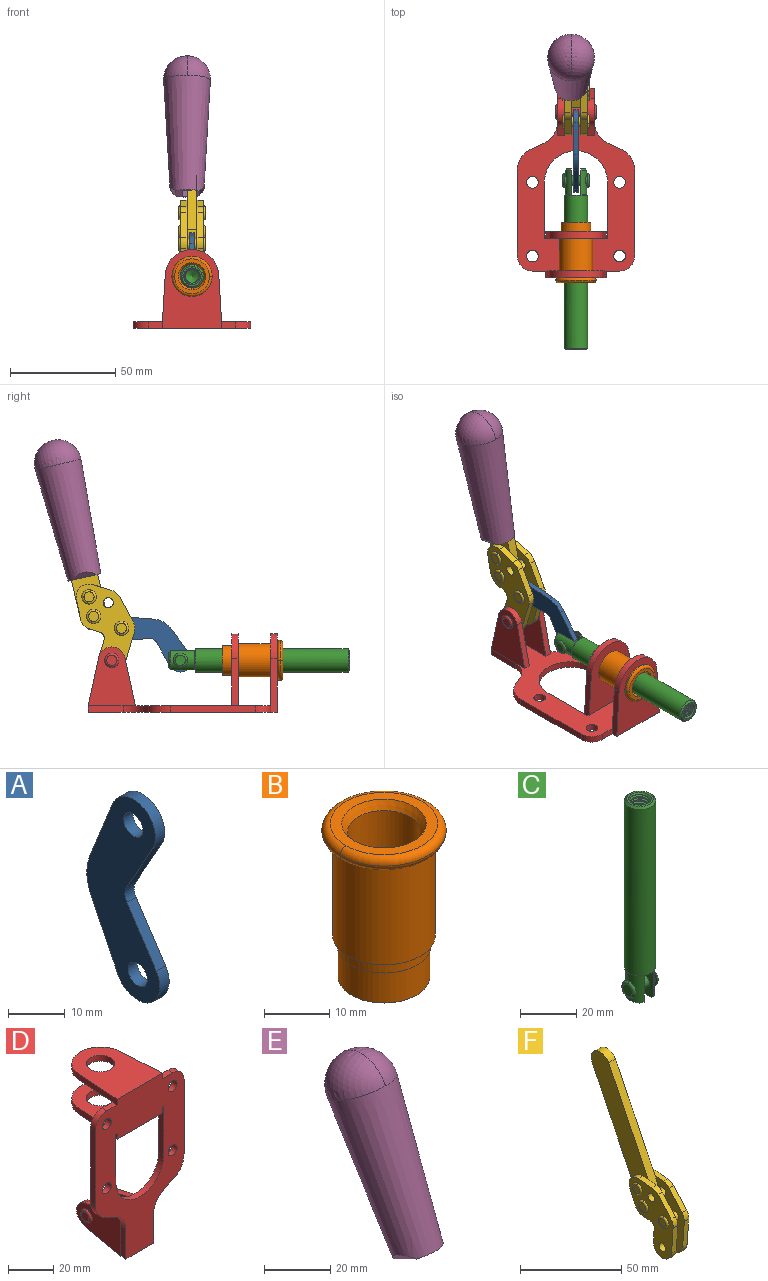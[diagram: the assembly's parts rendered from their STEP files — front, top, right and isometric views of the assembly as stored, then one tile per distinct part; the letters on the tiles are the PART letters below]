
ASSEMBLY  parts=6 mates=6
PART A: 12 faces, bbox 2.3x18.2x42.8 mm
  f0: cylinder r=2.4mm len=4.8mm, axis (1,0,0), area 34.9mm2, adj f4,f11
  f1: cylinder r=10.41mm len=8.47mm, axis (1,0,0), area 20.2mm2, adj f4,f9,f10,f11
  f2: cylinder r=3.05mm len=3.16mm, axis (1,0,0), area 7.7mm2, adj f4,f6,f7,f11
  f3: cylinder r=2.4mm len=4.8mm, axis (1,0,0), area 34.9mm2, adj f4,f11
  f4: plane 42.81x18.23mm, normal (-1,0,0), area 414.1mm2, adj f0,f1,f2,f3,f5,f6,f7,f8
  f5: cylinder r=5.54mm len=10.67mm, axis (1,0,0), area 41.8mm2, adj f4,f6,f10,f11
  f6: plane 11.66x6.53mm, normal (0,-0.87,-0.49), area 30.9mm2, adj f2,f4,f5,f11
  f7: plane 11.17x7.33mm, normal (0,-0.84,0.55), area 30.9mm2, adj f2,f4,f8,f11
  f8: cylinder r=5.54mm len=10.51mm, axis (1,0,0), area 41.8mm2, adj f4,f7,f9,f11
  f9: plane 13.67x6.67mm, normal (0,0.9,-0.44), area 35.1mm2, adj f1,f4,f8,f11
  f10: plane 14.1x5.7mm, normal (0,0.93,0.37), area 35.1mm2, adj f1,f4,f5,f11
  f11: plane 42.81x18.23mm, normal (1,0,0), area 414.1mm2, adj f0,f1,f2,f3,f5,f6,f7,f8
PART B: 15 faces, bbox 20.6x20.6x28.7 mm
  f0: torus R=8.26mm, axis (0,0,1), area 56.8mm2, adj f1,f10,f12
  f1: torus R=8.26mm, axis (0,0,1), area 56.8mm2, adj f0,f6,f13
  f2: cylinder r=5.59mm len=25.91mm, axis (0,0,1), area 909.6mm2, adj f3,f4
  f3: cone r=6.86mm half-angle=45deg, axis (0,0,-1), area 70.2mm2, adj f2,f14
  f4: cone r=6.47mm half-angle=30deg, axis (0,0,1), area 66.7mm2, adj f2,f13
  f5: cylinder r=7.04mm len=14.07mm, axis (0,0,1), area 252.6mm2, adj f11,f14
  f6: torus R=8.26mm, axis (0,0,1), area 56.8mm2, adj f1,f12,f13
  f7: cylinder r=7.16mm len=14.33mm, axis (0,0,1), area 91.5mm2, adj f9,f11
  f8: cylinder r=7.86mm len=18.42mm, axis (0,0,1), area 909.6mm2, adj f9,f10
  f9: plane 15.72x15.72mm, normal (0,0,-1), area 33mm2, adj f7,f8
  f10: plane 16.51x16.51mm, normal (0,0,-1), area 19.9mm2, adj f0,f8,f12
  f11: plane 14.33x14.33mm, normal (0,0,-1), area 5.7mm2, adj f5,f7
  f12: torus R=8.26mm, axis (0,0,1), area 56.8mm2, adj f0,f6,f10
  f13: plane 16.51x16.51mm, normal (0,0,1), area 82.7mm2, adj f1,f4,f6
  f14: plane 14.07x14.07mm, normal (0,0,-1), area 7.8mm2, adj f3,f5
PART C: 48 faces, bbox 12.6x11.1x86.1 mm
  f0: torus R=2.41mm, axis (-1,0,0), area 15mm2, adj f30,f32,f34
  f1: torus R=2.41mm, axis (-1,0,0), area 15mm2, adj f29,f31,f33
  f2: cylinder r=5.54mm len=72.39mm, axis (0,0,1), area 2518.5mm2, adj f3,f4,f42,f43
  f3: cone r=5.54mm half-angle=45deg, axis (0,0,1), area 7.6mm2, adj f2,f5,f41
  f4: cone r=5.54mm half-angle=45deg, axis (0,0,-1), area 34.9mm2, adj f2,f39
  f5: cylinder r=5.08mm len=11.48mm, axis (0,0,1), area 108.3mm2, adj f3,f7,f8,f41
  f6: cylinder r=2.41mm len=4.83mm, axis (-1,0,0), area 71.2mm2, adj f40,f41
  f7: cylinder r=2.41mm len=4.83mm, axis (-1,0,0), area 7.6mm2, adj f5,f34
  f8: cone r=5.08mm half-angle=45deg, axis (0,0,1), area 10.6mm2, adj f5,f37,f41
  f9: cone r=3.98mm half-angle=45deg, axis (0,0,1), area 17.6mm2, adj f27,f39,f45,f46,f47
  f10: cylinder r=2.41mm len=4.83mm, axis (-1,0,0), area 7.6mm2, adj f33,f38
  f11: cylinder r=3.2mm len=6.4mm, axis (0,0,1), area 78.4mm2, adj f12,f28,f44,f45,f47
  f12: cylinder r=3.2mm len=6.4mm, axis (0,0,1), area 10.5mm2, adj f11,f13,f45,f47
  f13: cylinder r=3.2mm len=6.4mm, axis (0,0,1), area 10.5mm2, adj f12,f14,f45,f47
  f14: cylinder r=3.2mm len=6.4mm, axis (0,0,1), area 10.5mm2, adj f13,f15,f45,f47
  f15: cylinder r=3.2mm len=6.4mm, axis (0,0,1), area 10.5mm2, adj f14,f16,f45,f47
  f16: cylinder r=3.2mm len=6.4mm, axis (0,0,1), area 10.5mm2, adj f15,f17,f45,f47
  f17: cylinder r=3.2mm len=6.4mm, axis (0,0,1), area 10.5mm2, adj f16,f18,f45,f47
  f18: cylinder r=3.2mm len=6.4mm, axis (0,0,1), area 10.5mm2, adj f17,f19,f45,f47
  f19: cylinder r=3.2mm len=6.4mm, axis (0,0,1), area 10.5mm2, adj f18,f20,f45,f47
  f20: cylinder r=3.2mm len=6.4mm, axis (0,0,1), area 10.5mm2, adj f19,f21,f45,f47
  f21: cylinder r=3.2mm len=6.4mm, axis (0,0,1), area 10.5mm2, adj f20,f22,f45,f47
  f22: cylinder r=3.2mm len=6.4mm, axis (0,0,1), area 10.5mm2, adj f21,f23,f45,f47
  f23: cylinder r=3.2mm len=6.4mm, axis (0,0,1), area 10.5mm2, adj f22,f24,f45,f47
  f24: cylinder r=3.2mm len=6.4mm, axis (0,0,1), area 10.5mm2, adj f23,f25,f45,f47
  f25: cylinder r=3.2mm len=6.4mm, axis (0,0,1), area 10.5mm2, adj f24,f26,f45,f47
  f26: cylinder r=3.2mm len=6.4mm, axis (0,0,1), area 10.5mm2, adj f25,f27,f45,f47
  f27: cylinder r=3.2mm len=6.4mm, axis (0,0,1), area 7.4mm2, adj f9,f26,f45,f47
  f28: cone r=3.2mm half-angle=60deg, axis (0,0,1), area 37.2mm2, adj f11
  f29: plane 4.83x4.83mm, normal (-1,0,0), area 18.3mm2, adj f1,f31
  f30: plane 4.83x4.83mm, normal (1,0,0), area 18.3mm2, adj f0,f32
  f31: torus R=2.41mm, axis (-1,0,0), area 15mm2, adj f1,f29,f33
  f32: torus R=2.41mm, axis (-1,0,0), area 15mm2, adj f0,f30,f34
  f33: plane 6.83x6.83mm, normal (1,0,0), area 18.3mm2, adj f1,f10,f31
  f34: plane 6.83x6.83mm, normal (-1,0,0), area 18.3mm2, adj f0,f7,f32
  f35: cone r=5.08mm half-angle=45deg, axis (0,0,1), area 10.6mm2, adj f36,f38,f40
  f36: plane 7.25x1.97mm, normal (0,0,-1), area 10mm2, adj f35,f40
  f37: plane 7.25x1.97mm, normal (0,0,-1), area 10mm2, adj f8,f41
  f38: cylinder r=5.08mm len=11.48mm, axis (0,0,1), area 108.3mm2, adj f10,f35,f40,f42
  f39: plane 9.55x9.55mm, normal (0,0,1), area 22mm2, adj f4,f9
  f40: plane 12.76x10.09mm, normal (1,0,0), area 95.7mm2, adj f6,f35,f36,f38,f42,f43
  f41: plane 12.76x10.09mm, normal (-1,0,0), area 95.7mm2, adj f3,f5,f6,f8,f37,f43
  f42: cone r=5.54mm half-angle=45deg, axis (0,0,1), area 7.6mm2, adj f2,f38,f40
  f43: plane 11.07x4.7mm, normal (0,0,-1), area 50.4mm2, adj f2,f40,f41
  f44: plane 0.89x0.62mm, normal (-1,0,0), area 0.3mm2, adj f11,f45,f46,f47
  f45: bspline ~24.8x7.63mm, area 266.6mm2, adj f9,f11,f12,f13,f14,f15,f16,f17
  f46: bspline ~24.87x7.63mm, area 73.6mm2, adj f9,f44,f45,f47
  f47: bspline ~24.98x7.63mm, area 272.5mm2, adj f9,f11,f12,f13,f14,f15,f16,f17
PART D: 55 faces, bbox 55.7x37.4x89.8 mm
  f0: torus R=2.41mm, axis (-1,0,0), area 15mm2, adj f11,f15,f25
  f1: torus R=2.41mm, axis (-1,0,0), area 15mm2, adj f10,f12,f22
  f2: cylinder r=2.78mm len=5.56mm, axis (0,-1,0), area 54.2mm2, adj f30,f54
  f3: cylinder r=14.99mm len=29.97mm, axis (0,-1,0), area 145.9mm2, adj f30,f49,f53,f54
  f4: cylinder r=2.78mm len=5.56mm, axis (0,-1,0), area 54.2mm2, adj f30,f54
  f5: cylinder r=2.78mm len=5.56mm, axis (0,-1,0), area 54.2mm2, adj f30,f54
  f6: cylinder r=2.78mm len=5.56mm, axis (0,-1,0), area 54.2mm2, adj f30,f54
  f7: cylinder r=6.35mm len=12.7mm, axis (0,0,1), area 123.6mm2, adj f27,f51
  f8: cylinder r=6.35mm len=12.7mm, axis (0,0,-1), area 124.7mm2, adj f21,f35
  f9: cylinder r=2.41mm len=11.18mm, axis (-1,0,0), area 169.4mm2, adj f16,f19
  f10: plane 4.83x4.83mm, normal (1,0,0), area 18.3mm2, adj f1,f12
  f11: plane 4.83x4.83mm, normal (-1,0,0), area 18.3mm2, adj f0,f15
  f12: torus R=2.41mm, axis (-1,0,0), area 15mm2, adj f1,f10,f22
  f13: cylinder r=6.35mm len=12.41mm, axis (1,0,0), area 53.4mm2, adj f18,f19,f22,f23
  f14: cylinder r=6.35mm len=12.41mm, axis (-1,0,0), area 53.4mm2, adj f16,f17,f24,f25
  f15: torus R=2.41mm, axis (-1,0,0), area 15mm2, adj f0,f11,f25
  f16: plane 27.86x22.35mm, normal (1,0,0), area 425.4mm2, adj f9,f14,f17,f24,f30
  f17: plane 22.86x4.97mm, normal (0,0.21,0.98), area 72.5mm2, adj f14,f16,f25,f30
  f18: plane 22.86x4.97mm, normal (0,0.21,0.98), area 72.5mm2, adj f13,f19,f22,f30
  f19: plane 27.86x22.35mm, normal (-1,0,0), area 425.4mm2, adj f9,f13,f18,f23,f30
  f20: cylinder r=12.7mm len=25.35mm, axis (0,0,-1), area 119.8mm2, adj f21,f34,f35,f36
  f21: plane 34.21x28.07mm, normal (0,0,-1), area 702.4mm2, adj f8,f20,f30,f34,f36
  f22: plane 27.96x22.45mm, normal (1,0,0), area 407.2mm2, adj f1,f12,f13,f18,f23,f30,f42,f43
  f23: plane 22.86x4.97mm, normal (0,0.21,-0.98), area 72.5mm2, adj f13,f19,f22,f44
  f24: plane 22.86x4.97mm, normal (0,0.21,-0.98), area 72.5mm2, adj f14,f16,f25,f44
  f25: plane 27.86x22.35mm, normal (-1,0,0), area 407.1mm2, adj f0,f14,f15,f17,f24,f30,f45,f46
  f26: plane 3.1x0.95mm, normal (0,0,-1), area 2.7mm2, adj f30,f49,f50,f54
  f27: plane 34.21x28.07mm, normal (0,0,1), area 702.4mm2, adj f7,f28,f30,f50,f52
  f28: cylinder r=12.7mm len=25.35mm, axis (0,0,1), area 118.8mm2, adj f27,f50,f51,f52
  f29: plane 3.1x0.95mm, normal (0,0,-1), area 2.7mm2, adj f30,f52,f53,f54
  f30: plane 86.54x55.63mm, normal (0,1,0), area 2362.9mm2, adj f2,f3,f4,f5,f6,f16,f17,f18
  f31: plane 40.56x3.1mm, normal (-1,0,0), area 125.7mm2, adj f30,f32,f48,f54
  f32: cylinder r=7.11mm len=7.11mm, axis (0,-1,0), area 34.6mm2, adj f30,f31,f33,f54
  f33: plane 6.67x3.1mm, normal (0,0,1), area 20.4mm2, adj f30,f32,f34,f54
  f34: plane 25.39x3.13mm, normal (-1,0.06,0), area 79.5mm2, adj f20,f21,f33,f35,f54
  f35: plane 37.31x28.45mm, normal (0,0,1), area 789.9mm2, adj f8,f20,f34,f36,f54
  f36: plane 25.39x3.13mm, normal (1,0.06,0), area 79.5mm2, adj f20,f21,f35,f37,f54
  f37: plane 6.67x3.1mm, normal (0,0,1), area 20.4mm2, adj f30,f36,f38,f54
  f38: cylinder r=7.11mm len=7.11mm, axis (0,-1,0), area 34.6mm2, adj f30,f37,f39,f54
  f39: plane 40.56x3.1mm, normal (1,0,0), area 125.7mm2, adj f30,f38,f40,f54
  f40: cylinder r=11.18mm len=10.16mm, axis (0,-1,0), area 39.5mm2, adj f30,f39,f41,f54
  f41: plane 6.09x3.1mm, normal (0.42,0,-0.91), area 20.8mm2, adj f30,f40,f42,f54
  f42: cylinder r=11.18mm len=9.41mm, axis (0,-1,0), area 37.2mm2, adj f22,f30,f41,f43,f54
  f43: plane 16.5x3.1mm, normal (1,0,0), area 51.1mm2, adj f22,f42,f44,f54
  f44: plane 17.37x3.1mm, normal (0,0,-1), area 53.8mm2, adj f23,f24,f30,f43,f45,f54
  f45: plane 16.5x3.1mm, normal (-1,0,0), area 51.1mm2, adj f25,f44,f46,f54
  f46: cylinder r=11.18mm len=9.41mm, axis (0,-1,0), area 37.2mm2, adj f25,f30,f45,f47,f54
  f47: plane 6.09x3.1mm, normal (-0.42,0,-0.91), area 20.8mm2, adj f30,f46,f48,f54
  f48: cylinder r=11.18mm len=10.16mm, axis (0,-1,0), area 39.5mm2, adj f30,f31,f47,f54
  f49: plane 26.54x3.1mm, normal (-1,0,0), area 82.3mm2, adj f3,f26,f30,f54
  f50: plane 25.39x3.1mm, normal (1,0.06,0), area 78.8mm2, adj f26,f27,f28,f51,f54
  f51: plane 37.31x28.45mm, normal (0,0,-1), area 789.9mm2, adj f7,f28,f50,f52,f54
  f52: plane 25.39x3.1mm, normal (-1,0.06,0), area 78.8mm2, adj f27,f28,f29,f51,f54
  f53: plane 26.54x3.1mm, normal (1,0,0), area 82.3mm2, adj f3,f29,f30,f54
  f54: plane 89.66x55.63mm, normal (0,-1,0), area 2678.5mm2, adj f2,f3,f4,f5,f6,f26,f29,f31
PART E: 11 faces, bbox 22.3x42.6x64.5 mm
  f0: sphere r=11.13mm, area 411.4mm2, adj f1,f8
  f1: cone r=11.11mm half-angle=3.3deg, axis (0,0.44,0.9), area 3251.8mm2, adj f0,f7,f8,f9,f10
  f2: cylinder r=6.16mm len=11.7mm, axis (1,0,0), area 89.5mm2, adj f3,f4,f5,f6
  f3: plane 60.23x36.75mm, normal (-1,0,0), area 763.6mm2, adj f2,f4,f6,f10
  f4: plane 51.37x25.05mm, normal (0,0.9,-0.44), area 264.2mm2, adj f2,f3,f5,f10
  f5: plane 60.23x36.75mm, normal (1,0,0), area 763.6mm2, adj f2,f4,f6,f10
  f6: plane 51.37x25.05mm, normal (0,-0.9,0.44), area 264.2mm2, adj f2,f3,f5,f10
  f7: plane 9.95x5.95mm, normal (0.71,-0.31,-0.64), area 25.8mm2, adj f1,f10
  f8: sphere r=11.13mm, area 411.4mm2, adj f0,f1
  f9: plane 9.95x5.95mm, normal (-0.71,-0.31,-0.64), area 25.8mm2, adj f1,f10
  f10: plane 14.27x11.38mm, normal (0,-0.44,-0.9), area 106.7mm2, adj f1,f3,f4,f5,f6,f7,f9
PART F: 59 faces, bbox 12.9x60.2x99.6 mm
  f0: torus R=2.39mm, axis (-1,0,0), area 14.9mm2, adj f20,f43,f51
  f1: torus R=2.39mm, axis (-1,0,0), area 14.9mm2, adj f19,f42,f51
  f2: torus R=2.39mm, axis (-1,0,0), area 14.9mm2, adj f18,f35,f51
  f3: torus R=2.39mm, axis (-1,0,0), area 14.9mm2, adj f14,f17,f23
  f4: torus R=2.39mm, axis (-1,0,0), area 14.9mm2, adj f13,f16,f23
  f5: torus R=2.39mm, axis (-1,0,0), area 14.9mm2, adj f12,f15,f23
  f6: cylinder r=2.39mm len=4.78mm, axis (1,0,0), area 46.5mm2, adj f48,f50,f51
  f7: cylinder r=2.39mm len=4.78mm, axis (1,0,0), area 46.5mm2, adj f50,f51
  f8: cylinder r=6.35mm len=12.68mm, axis (1,0,0), area 61.8mm2, adj f38,f39,f50,f51
  f9: cylinder r=2.39mm len=4.78mm, axis (-1,0,0), area 70.5mm2, adj f46,f50
  f10: cylinder r=2.39mm len=4.78mm, axis (-1,0,0), area 46.5mm2, adj f23,f45,f46
  f11: cylinder r=2.39mm len=4.78mm, axis (-1,0,0), area 46.5mm2, adj f23,f46
  f12: plane 4.78x4.78mm, normal (1,0,0), area 17.9mm2, adj f5,f15
  f13: plane 4.78x4.78mm, normal (1,0,0), area 17.9mm2, adj f4,f16
  f14: plane 4.78x4.78mm, normal (1,0,0), area 17.9mm2, adj f3,f17
  f15: torus R=2.39mm, axis (-1,0,0), area 14.9mm2, adj f5,f12,f23
  f16: torus R=2.39mm, axis (-1,0,0), area 14.9mm2, adj f4,f13,f23
  f17: torus R=2.39mm, axis (-1,0,0), area 14.9mm2, adj f3,f14,f23
  f18: plane 4.78x4.78mm, normal (-1,0,0), area 17.9mm2, adj f2,f35
  f19: plane 4.78x4.78mm, normal (-1,0,0), area 17.9mm2, adj f1,f42
  f20: plane 4.78x4.78mm, normal (-1,0,0), area 17.9mm2, adj f0,f43
  f21: plane 2.26x0.2mm, normal (1,0,0), area 0.2mm2, adj f31,f44
  f22: plane 2.26x0.2mm, normal (-1,0,0), area 0.2mm2, adj f41,f44
  f23: plane 39.37x30.77mm, normal (1,0,0), area 565.5mm2, adj f3,f4,f5,f10,f11,f15,f16,f17
  f24: cylinder r=6.1mm len=4.15mm, axis (-1,0,0), area 14.7mm2, adj f23,f25,f32,f46
  f25: plane 10.25x9.01mm, normal (0,-0.75,0.66), area 42.3mm2, adj f23,f24,f26,f46
  f26: cylinder r=6.35mm len=4.64mm, axis (-1,0,0), area 15.6mm2, adj f23,f25,f27,f46
  f27: plane 15.84x3.1mm, normal (0,-1,-0.07), area 49.2mm2, adj f23,f26,f28,f46
  f28: cylinder r=6.35mm len=12.68mm, axis (-1,0,0), area 61.8mm2, adj f23,f27,f29,f46
  f29: plane 8.11x3.1mm, normal (0,1,0.07), area 25.2mm2, adj f23,f28,f30,f46
  f30: cylinder r=3.05mm len=3.25mm, axis (-1,0,0), area 14.8mm2, adj f23,f29,f31,f46
  f31: plane 5.99x3.1mm, normal (0,0.07,-1), area 18.6mm2, adj f21,f23,f30,f44,f46
  f32: plane 9.5x3.1mm, normal (0,-0.07,1), area 29.5mm2, adj f23,f24,f33,f46,f47
  f33: cylinder r=6.1mm len=8.63mm, axis (-1,0,0), area 39.1mm2, adj f23,f32,f34,f47
  f34: plane 8.65x3.96mm, normal (0,0.91,-0.42), area 29.5mm2, adj f23,f33,f44,f47
  f35: torus R=2.39mm, axis (-1,0,0), area 14.9mm2, adj f2,f18,f51
  f36: plane 10.25x9.01mm, normal (0,-0.75,0.66), area 42.3mm2, adj f37,f49,f50,f51
  f37: cylinder r=6.35mm len=4.64mm, axis (1,0,0), area 15.6mm2, adj f36,f38,f50,f51
  f38: plane 15.84x3.1mm, normal (0,-1,-0.07), area 49.2mm2, adj f8,f37,f50,f51
  f39: plane 8.11x3.1mm, normal (0,1,0.07), area 25.2mm2, adj f8,f40,f50,f51
  f40: cylinder r=3.05mm len=3.25mm, axis (1,0,0), area 14.8mm2, adj f39,f41,f50,f51
  f41: plane 5.99x3.1mm, normal (0,0.07,-1), area 18.6mm2, adj f22,f40,f44,f50,f51
  f42: torus R=2.39mm, axis (-1,0,0), area 14.9mm2, adj f1,f19,f51
  f43: torus R=2.39mm, axis (-1,0,0), area 14.9mm2, adj f0,f20,f51
  f44: cylinder r=6.35mm len=12.12mm, axis (-1,0,0), area 128.9mm2, adj f21,f22,f23,f31,f34,f41,f46,f47
  f45: plane 2.65x1.35mm, normal (1,0,0), area 1mm2, adj f10,f55
  f46: plane 39.08x20.42mm, normal (-1,0,0), area 412.5mm2, adj f9,f10,f11,f24,f25,f26,f27,f28
  f47: plane 77.62x39.82mm, normal (1,0,0), area 850mm2, adj f32,f33,f34,f44,f53,f54,f55
  f48: plane 2.65x1.35mm, normal (-1,0,0), area 1mm2, adj f6,f55
  f49: cylinder r=6.1mm len=4.15mm, axis (1,0,0), area 14.7mm2, adj f36,f50,f51,f56
  f50: plane 39.08x20.42mm, normal (1,0,0), area 412.5mm2, adj f6,f7,f8,f9,f36,f37,f38,f39
  f51: plane 39.37x30.77mm, normal (-1,0,0), area 565.5mm2, adj f0,f1,f2,f6,f7,f8,f35,f36
  f52: plane 8.65x3.96mm, normal (0,0.91,-0.42), area 29.5mm2, adj f44,f51,f57,f58
  f53: plane 68.49x33.4mm, normal (0,0.9,-0.44), area 358.1mm2, adj f44,f47,f54,f58
  f54: cylinder r=6.35mm len=12.06mm, axis (1,0,0), area 93.7mm2, adj f47,f53,f55,f58
  f55: plane 68.49x33.4mm, normal (0,-0.9,0.44), area 358.1mm2, adj f44,f45,f46,f47,f48,f50,f54,f58
  f56: plane 9.5x3.1mm, normal (0,-0.07,1), area 29.5mm2, adj f49,f50,f51,f57,f58
  f57: cylinder r=6.1mm len=8.63mm, axis (1,0,0), area 39.1mm2, adj f51,f52,f56,f58
  f58: plane 77.62x39.82mm, normal (-1,0,0), area 850mm2, adj f44,f52,f53,f54,f55,f56,f57
PLACE A rot(axis=(1,0,0),120.6deg) t=(0,34.6,11.3)mm
PLACE B rot(axis=(1,0,0),90deg) t=(0,9.14,0)mm
PLACE C rot(axis=(1,0,0),90deg) t=(0,24.23,0)mm
PLACE D rot(axis=(1,0,0),90deg) t=(0,9.14,0)mm fixed
PLACE E rot(axis=(1,0,0),12.9deg) t=(-2.35,10.1,50.43)mm
PLACE F rot(axis=(1,0,0),12.9deg) t=(0,10.1,50.43)mm
MATE fastened B.f2 <-> D.f7  axis (0,1,0) through (0,-37.25,24.61)mm
MATE revolute A.f5 <-> C.f6  axis (1,0,0) through (0,8.75,24.61)mm
MATE slider C.f2 <-> B.f2  axis (0,-1,0) through (0,-34.55,24.61)mm
MATE revolute A.f3 <-> F.f4  axis (1,0,0) through (0,36.63,39.81)mm
MATE fastened F.f54 <-> E.f2  axis (-1,0,0) through (-2.35,67.18,119.63)mm
MATE revolute D.f0 <-> F.f7  axis (-1,0,0) through (0,41.23,24.61)mm
